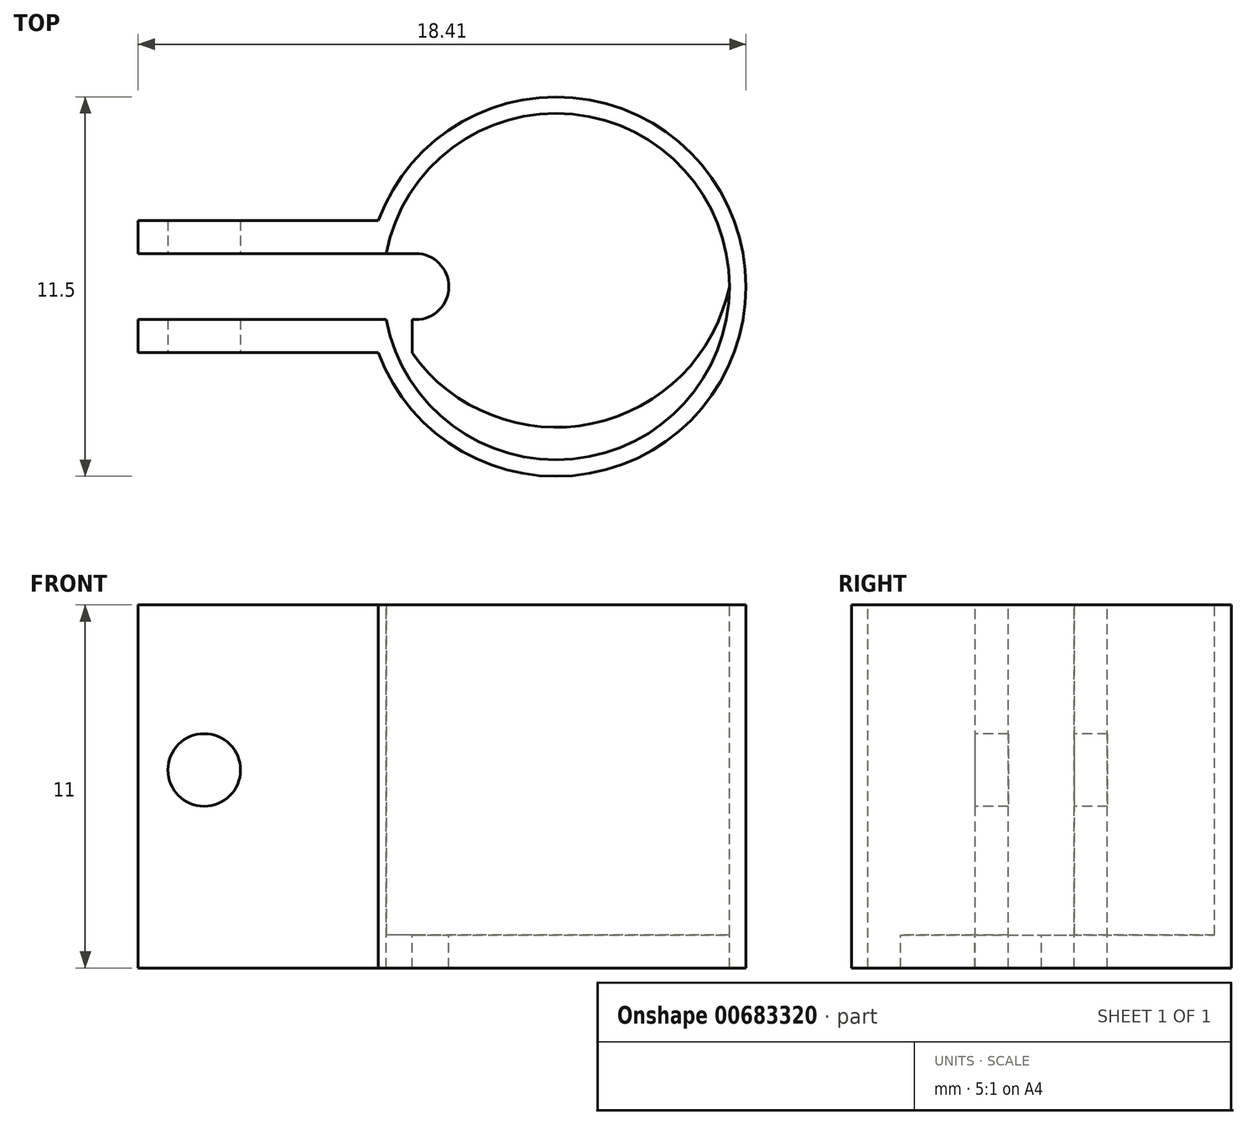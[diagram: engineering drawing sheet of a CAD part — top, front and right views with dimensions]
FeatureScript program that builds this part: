
annotation { "Feature Type Name" : "Feature", "Feature Type Description" : "" }
export const myFeature = defineFeature(function(context is Context, id is Id, definition is map)
    precondition{}
    {
        {
            var Q0;
            Q0=qCreatedBy(makeId("Top.planeOp"),FACE);
            var sketch = newSketch(context, id + "F0", { "sketchPlane" : qUnion([Q0])});
            skCircle(sketch, "E0", {"center": v(0, 0) * mm, "radius": 5.25 * mm});
            skCircle(sketch, "E1", {"center": v(0, 0) * mm, "radius": 4.25 * mm, "construction": true});
            skLineSegment(sketch, "E2", {"start": v(0, 0) * mm, "end": v(-4.25, 0) * mm, "construction": true});
            skCircle(sketch, "E3", {"center": v(-4.25, 0) * mm, "radius": 1 * mm});
            skLineSegment(sketch, "E4", {"start": v(-4.25, 0) * mm, "end": v(-4.25, 1) * mm, "construction": true});
            skLineSegment(sketch, "E5", {"start": v(-4.25, 1) * mm, "end": v(-4.25, -1) * mm, "construction": true});
            skLineSegment(sketch, "E6", {"start": v(-4.25, 1) * mm, "end": v(-5.15, 1) * mm});
            skLineSegment(sketch, "E7", {"start": v(-4.25, -1) * mm, "end": v(-5.15, -1) * mm});
            skCircle(sketch, "E8", {"center": v(0, 0) * mm, "radius": 5.75 * mm});
            skLineSegment(sketch, "E9", {"start": v(0, 0) * mm, "end": v(5.25, 0) * mm, "construction": true});
            skLineSegment(sketch, "E10", {"start": v(-4.25, 0) * mm, "end": v(-5.75, 0) * mm, "construction": true});
            skArc(sketch, "E11", {"start": v(-5.25, 0) * mm, "mid": v(0, -4.26) * mm, "end": v(5.25, 0) * mm});
            skLineSegment(sketch, "E12", {"start": v(-5.15, -1) * mm, "end": v(-5.66, -1) * mm});
            skLineSegment(sketch, "E13", {"start": v(-5.15, 1) * mm, "end": v(-5.66, 1) * mm});
            skLineSegment(sketch, "E14.bottom", {"start": v(-5.66, 1) * mm, "end": v(-12.66, 1) * mm});
            skLineSegment(sketch, "E14.top", {"start": v(-5.66, 2) * mm, "end": v(-12.66, 2) * mm});
            skLineSegment(sketch, "E14.left", {"start": v(-5.66, 1) * mm, "end": v(-5.66, 2) * mm});
            skLineSegment(sketch, "E14.right", {"start": v(-12.66, 1) * mm, "end": v(-12.66, 2) * mm});
            skLineSegment(sketch, "E15", {"start": v(-5.66, 2) * mm, "end": v(-4.65, 2) * mm});
            skLineSegment(sketch, "E16.bottom", {"start": v(-5.66, -1) * mm, "end": v(-12.66, -1) * mm});
            skLineSegment(sketch, "E16.top", {"start": v(-5.66, -2) * mm, "end": v(-12.66, -2) * mm});
            skLineSegment(sketch, "E16.left", {"start": v(-5.66, -1) * mm, "end": v(-5.66, -2) * mm});
            skLineSegment(sketch, "E16.right", {"start": v(-12.66, -1) * mm, "end": v(-12.66, -2) * mm});
            skLineSegment(sketch, "E17", {"start": v(-5.66, -2) * mm, "end": v(-4.74, -2) * mm});
            skLineSegment(sketch, "E18", {"start": v(0, 1.1) * mm, "end": v(0, 0) * mm});
            skSolve(sketch);
        }
        {
            var Q0;
            {var subQ5=sQuery(id+"F0.wireOp",EDGE,"E6");Q0=makeQuery(id+"F0.imprint","IMPRINT",FACE,{"disambiguationData":[TD([[makeQuery(id+"F0.imprint","IMPRINT",EDGE,{"derivedFrom":subQ5}),-1.0]])]});}
            var Q1;
            {var subQ0=sQuery(id+"F0.wireOp",EDGE,"E12");Q1=makeQuery(id+"F0.imprint","IMPRINT",FACE,{"disambiguationData":[TD([[makeQuery(id+"F0.imprint","IMPRINT",EDGE,{"derivedFrom":subQ0}),1.0]])]});}
            var Q2;
            {var subQ0=sQuery(id+"F0.wireOp",EDGE,"E16.left");Q2=makeQuery(id+"F0.imprint","IMPRINT",FACE,{"disambiguationData":[TD([[makeQuery(id+"F0.imprint","IMPRINT",EDGE,{"derivedFrom":subQ0}),1.0]])]});}
            var Q3;
            Q3=makeQuery(id+"F0.imprint","IMPRINT",FACE,{"disambiguationData":[TD([[makeQuery(id+"F0.imprint","IMPRINT",EDGE,{"derivedFrom":sQuery(id+"F0.wireOp",EDGE,"E16.bottom")}),1.0]])]});
            var Q4;
            Q4=makeQuery(id+"F0.imprint","IMPRINT",FACE,{"disambiguationData":[TD([[makeQuery(id+"F0.imprint","IMPRINT",EDGE,{"derivedFrom":sQuery(id+"F0.wireOp",EDGE,"E14.bottom")}),-1.0]])]});
            var Q5;
            {var subQ0=sQuery(id+"F0.wireOp",EDGE,"E14.left");Q5=makeQuery(id+"F0.imprint","IMPRINT",FACE,{"disambiguationData":[TD([[makeQuery(id+"F0.imprint","IMPRINT",EDGE,{"derivedFrom":subQ0}),-1.0]])]});}
            var Q6;
            {var subQ0=sQuery(id+"F0.wireOp",EDGE,"E13");Q6=makeQuery(id+"F0.imprint","IMPRINT",FACE,{"disambiguationData":[TD([[makeQuery(id+"F0.imprint","IMPRINT",EDGE,{"derivedFrom":subQ0}),-1.0]])]});}
            var Q7;
            {var subQ1=sQuery(id+"F0.wireOp",EDGE,"E0");var subQ7=makeQuery(id+"F0.imprint","INTERSECT",VERTEX,{"disambiguationData":[OD(1.0)],"derivedFrom":[subQ1,sQuery(id+"F0.wireOp",EDGE,"E11")]});Q7=makeQuery(id+"F0.imprint","IMPRINT",FACE,{"disambiguationData":[TD([[makeQuery(id+"F0.imprint","IMPRINT",EDGE,{"disambiguationData":[TD([[subQ7,-1.0]])],"derivedFrom":subQ1}),-1.0]])]});}
            extrude(context, id + "F1", {"entities" : qUnion([Q0, Q1, Q2, Q3, Q4, Q5, Q6, Q7]), "oppositeDirection" : true, "depth" : 1 * mm, "offsetDistance" : 25 * mm});
        }
        {
            var Q0;
            {var subQ0=sQuery(id+"F0.wireOp",EDGE,"E12");Q0=makeQuery(id+"F0.imprint","IMPRINT",FACE,{"disambiguationData":[TD([[makeQuery(id+"F0.imprint","IMPRINT",EDGE,{"derivedFrom":subQ0}),1.0]])]});}
            var Q1;
            Q1=makeQuery(id+"F0.imprint","IMPRINT",FACE,{"disambiguationData":[TD([[makeQuery(id+"F0.imprint","IMPRINT",EDGE,{"derivedFrom":sQuery(id+"F0.wireOp",EDGE,"E16.bottom")}),1.0]])]});
            var Q2;
            Q2=makeQuery(id+"F0.imprint","IMPRINT",FACE,{"disambiguationData":[TD([[makeQuery(id+"F0.imprint","IMPRINT",EDGE,{"derivedFrom":sQuery(id+"F0.wireOp",EDGE,"E14.bottom")}),-1.0]])]});
            var Q3;
            {var subQ0=sQuery(id+"F0.wireOp",EDGE,"E14.left");Q3=makeQuery(id+"F0.imprint","IMPRINT",FACE,{"disambiguationData":[TD([[makeQuery(id+"F0.imprint","IMPRINT",EDGE,{"derivedFrom":subQ0}),-1.0]])]});}
            var Q4;
            {var subQ0=sQuery(id+"F0.wireOp",EDGE,"E16.left");Q4=makeQuery(id+"F0.imprint","IMPRINT",FACE,{"disambiguationData":[TD([[makeQuery(id+"F0.imprint","IMPRINT",EDGE,{"derivedFrom":subQ0}),1.0]])]});}
            var Q5;
            {var subQ1=sQuery(id+"F0.wireOp",EDGE,"E0");var subQ7=makeQuery(id+"F0.imprint","INTERSECT",VERTEX,{"disambiguationData":[OD(1.0)],"derivedFrom":[subQ1,sQuery(id+"F0.wireOp",EDGE,"E11")]});Q5=makeQuery(id+"F0.imprint","IMPRINT",FACE,{"disambiguationData":[TD([[makeQuery(id+"F0.imprint","IMPRINT",EDGE,{"disambiguationData":[TD([[subQ7,-1.0]])],"derivedFrom":subQ1}),-1.0]])]});}
            var Q6;
            {var subQ0=sQuery(id+"F0.wireOp",EDGE,"E13");Q6=makeQuery(id+"F0.imprint","IMPRINT",FACE,{"disambiguationData":[TD([[makeQuery(id+"F0.imprint","IMPRINT",EDGE,{"derivedFrom":subQ0}),-1.0]])]});}
            extrude(context, id + "F2", {"entities" : qUnion([Q0, Q1, Q2, Q3, Q4, Q5, Q6]), "operationType" : NewBodyOperationType.ADD, "depth" : 10 * mm, "offsetDistance" : 25 * mm});
        }
        {
            var Q0;
            {var subQ0=sQuery(id+"F0.wireOp",EDGE,"E17");var subQ1=sQuery(id+"F0.wireOp",EDGE,"E16.top");Q0=makeQuery(id+"F2.boolean.opBoolean","MERGE",FACE,{"derivedFrom":[makeQuery(id+"F1.opExtrude","SWEPT_FACE",FACE,{"disambiguationData":[OSD([subQ1,subQ0])]}),makeQuery(id+"F2.opExtrude","SWEPT_FACE",FACE,{"disambiguationData":[OSD([subQ1,subQ0])]})]});}
            var sketch = newSketch(context, id + "F3", { "sketchPlane" : qUnion([Q0])});
            skLineSegment(sketch, "E19", {"start": v(-12.66, 10) * mm, "end": v(-12.66, 0) * mm});
            skLineSegment(sketch, "E20", {"start": v(-12.66, 5) * mm, "end": v(-10.66, 5) * mm});
            skCircle(sketch, "E21", {"center": v(-10.66, 5) * mm, "radius": 1.1 * mm});
            skCircle(sketch, "E22", {"center": v(-10.66, 5) * mm, "radius": 2 * mm});
            skSolve(sketch);
        }
        {
            var Q0;
            Q0=makeQuery(id+"F3.imprint","IMPRINT",FACE,{"disambiguationData":[TD([[makeQuery(id+"F3.imprint","IMPRINT",EDGE,{"derivedFrom":sQuery(id+"F3.wireOp",EDGE,"E21")}),1.0]])]});
            extrude(context, id + "F4", {"entities" : qUnion([Q0]), "operationType" : NewBodyOperationType.REMOVE, "oppositeDirection" : true, "depth" : 25 * mm, "offsetDistance" : 25 * mm});
        }
        {
            var Q0;
            {var subQ0=sQuery(id+"F0.wireOp",EDGE,"E6");Q0=makeQuery(id+"F0.imprint","IMPRINT",FACE,{"disambiguationData":[TD([[makeQuery(id+"F0.imprint","IMPRINT",EDGE,{"derivedFrom":subQ0}),-1.0]])]});}
            var sketch = newSketch(context, id + "F5", { "sketchPlane" : qUnion([Q0])});
            skLineSegment(sketch, "E23", {"start": v(-4.6, -2.28) * mm, "end": v(-5.14, -0.9) * mm});
            skLineSegment(sketch, "E24", {"start": v(-5.14, -0.9) * mm, "end": v(-4.37, -0.9) * mm});
            skLineSegment(sketch, "E25", {"start": v(-4.37, -0.9) * mm, "end": v(-4.37, -2.5) * mm});
            skLineSegment(sketch, "E26", {"start": v(-4.37, -2.5) * mm, "end": v(-4.6, -2.28) * mm});
            skSolve(sketch);
        }
        {
            var Q0;
            Q0 = qSketchRegion(id + "F5", true);
            extrude(context, id + "F6", {"entities" : qUnion([Q0]), "operationType" : NewBodyOperationType.REMOVE, "endBound" : BoundingType.SYMMETRIC, "oppositeDirection" : true, "depth" : 25 * mm, "offsetDistance" : 25 * mm});
        }
    });
